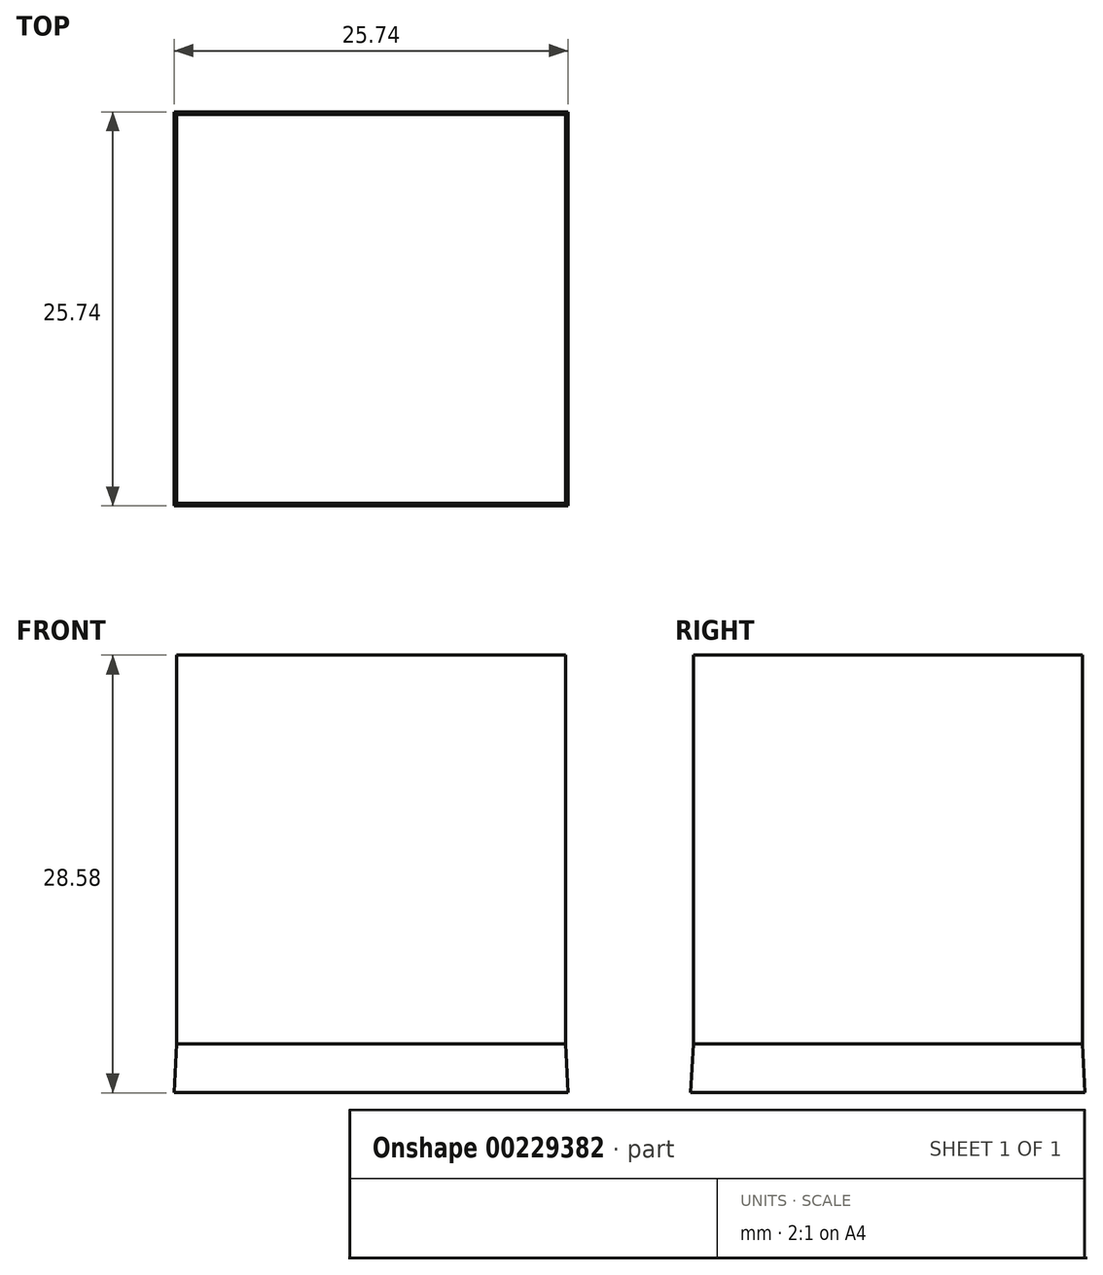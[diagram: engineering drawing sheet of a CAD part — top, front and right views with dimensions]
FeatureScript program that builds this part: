
annotation { "Feature Type Name" : "Feature", "Feature Type Description" : "" }
export const myFeature = defineFeature(function(context is Context, id is Id, definition is map)
    precondition{}
    {
        {
            var Q0;
            Q0=qCreatedBy(makeId("Top.planeOp"),FACE);
            var sketch = newSketch(context, id + "F0", { "sketchPlane" : qUnion([Q0])});
            skLineSegment(sketch, "E0.bottom", {"start": v(12.7, 12.7) * mm, "end": v(-12.7, 12.7) * mm});
            skLineSegment(sketch, "E0.top", {"start": v(12.7, -12.7) * mm, "end": v(-12.7, -12.7) * mm});
            skLineSegment(sketch, "E0.left", {"start": v(12.7, 12.7) * mm, "end": v(12.7, -12.7) * mm});
            skLineSegment(sketch, "E0.right", {"start": v(-12.7, 12.7) * mm, "end": v(-12.7, -12.7) * mm});
            skPoint(sketch, "E0.middle", {"position": v(0, 0) * mm});
            skSolve(sketch);
        }
        {
            var Q0;
            Q0 = qSketchRegion(id + "F0", true);
            extrude(context, id + "F1", {"entities" : qUnion([Q0]), "oppositeDirection" : true, "depth" : 3.17 * mm, "hasDraft" : true, "draftAngle" : 3 * degree});
        }
        {
            var Q0;
            Q0=makeQuery(id+"F1.opExtrude","CAP_FACE",FACE,{"disambiguationData":[OSD([sQuery(id+"F0.wireOp",EDGE,"E0.bottom"),sQuery(id+"F0.wireOp",EDGE,"E0.top"),sQuery(id+"F0.wireOp",EDGE,"E0.left"),sQuery(id+"F0.wireOp",EDGE,"E0.right")])],"isStart":true});
            extrude(context, id + "F2", {"entities" : qUnion([Q0]), "operationType" : NewBodyOperationType.ADD, "depth" : 25.4 * mm});
        }
    });
